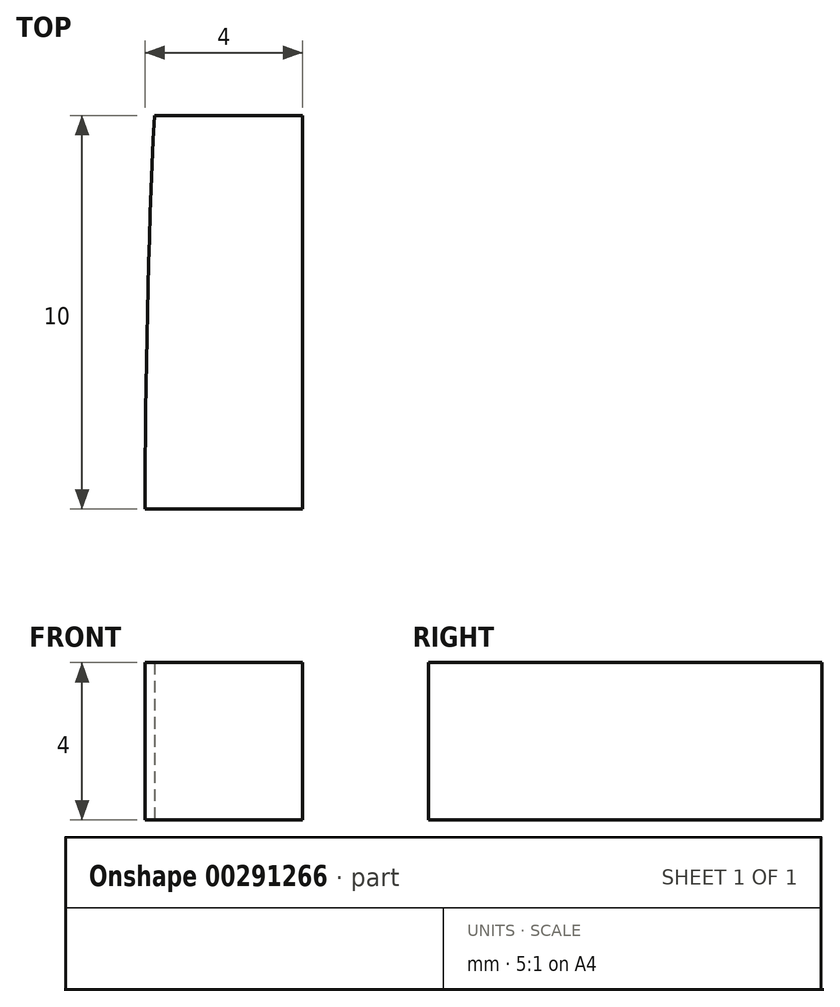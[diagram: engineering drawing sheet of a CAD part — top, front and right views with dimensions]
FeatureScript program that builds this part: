
annotation { "Feature Type Name" : "Feature", "Feature Type Description" : "" }
export const myFeature = defineFeature(function(context is Context, id is Id, definition is map)
    precondition{}
    {
        {
            var Q0;
            Q0=qCreatedBy(makeId("Top.planeOp"),FACE);
            var sketch = newSketch(context, id + "F0", { "sketchPlane" : qUnion([Q0])});
            skArc(sketch, "E0", {"start": v(-134.47, 163.78) * mm, "mid": v(-211.91, 0) * mm, "end": v(-134.47, -163.78) * mm});
            skLineSegment(sketch, "E1.bottom", {"start": v(-134.47, -163.78) * mm, "end": v(-132, -163.78) * mm});
            skLineSegment(sketch, "E1.top", {"start": v(-134.47, 163.78) * mm, "end": v(-132, 163.78) * mm});
            skArc(sketch, "E2.trimOffspring", {"start": v(134.47, -163.78) * mm, "mid": v(211.91, 0) * mm, "end": v(134.47, 163.78) * mm});
            skPoint(sketch, "E1.right.start.orphan", {"position": v(234.51, -163.78) * mm});
            skPoint(sketch, "E3.orphan", {"position": v(234.51, 163.78) * mm});
            skPoint(sketch, "E1.left.end.orphan", {"position": v(-234.51, 163.78) * mm});
            skPoint(sketch, "E4.orphan", {"position": v(-234.51, -163.78) * mm});
            skLineSegment(sketch, "E5.bottom", {"start": v(-40, 120) * mm, "end": v(40, 120) * mm});
            skLineSegment(sketch, "E5.top", {"start": v(-40, 140) * mm, "end": v(40, 140) * mm});
            skLineSegment(sketch, "E5.left", {"start": v(-40, 120) * mm, "end": v(-40, 140) * mm});
            skLineSegment(sketch, "E5.right", {"start": v(40, 120) * mm, "end": v(40, 140) * mm});
            skPoint(sketch, "E5.middle", {"position": v(0, 130) * mm});
            skLineSegment(sketch, "E6.bottom", {"start": v(-40, -140) * mm, "end": v(40, -140) * mm});
            skLineSegment(sketch, "E6.top", {"start": v(-40, -120) * mm, "end": v(40, -120) * mm});
            skLineSegment(sketch, "E6.left", {"start": v(-40, -140) * mm, "end": v(-40, -120) * mm});
            skLineSegment(sketch, "E6.right", {"start": v(40, -140) * mm, "end": v(40, -120) * mm});
            skPoint(sketch, "E6.middle", {"position": v(0, -130) * mm});
            skLineSegment(sketch, "E7", {"start": v(0, 163.78) * mm, "end": v(0, 159.78) * mm});
            skPoint(sketch, "E7.endSnap0", {"position": v(0, 163.78) * mm});
            skLineSegment(sketch, "E8", {"start": v(0, 159.78) * mm, "end": v(15, 159.78) * mm});
            skLineSegment(sketch, "E9", {"start": v(15, 159.78) * mm, "end": v(15, 163.78) * mm});
            skLineSegment(sketch, "E10.1.0.0", {"start": v(34.4, 159.78) * mm, "end": v(34.4, 163.78) * mm});
            skLineSegment(sketch, "E10.1.0.1", {"start": v(19.4, 159.78) * mm, "end": v(34.4, 159.78) * mm});
            skLineSegment(sketch, "E10.1.0.2", {"start": v(19.4, 163.78) * mm, "end": v(19.4, 159.78) * mm});
            skLineSegment(sketch, "E10.2.0.0", {"start": v(53.8, 159.78) * mm, "end": v(53.8, 163.78) * mm});
            skLineSegment(sketch, "E10.2.0.1", {"start": v(38.8, 159.78) * mm, "end": v(53.8, 159.78) * mm});
            skLineSegment(sketch, "E10.2.0.2", {"start": v(38.8, 163.78) * mm, "end": v(38.8, 159.78) * mm});
            skLineSegment(sketch, "E10.3.0.0", {"start": v(73.2, 159.78) * mm, "end": v(73.2, 163.78) * mm});
            skLineSegment(sketch, "E10.3.0.1", {"start": v(58.2, 159.78) * mm, "end": v(73.2, 159.78) * mm});
            skLineSegment(sketch, "E10.3.0.2", {"start": v(58.2, 163.78) * mm, "end": v(58.2, 159.78) * mm});
            skLineSegment(sketch, "E10.4.0.0", {"start": v(92.6, 159.78) * mm, "end": v(92.6, 163.78) * mm});
            skLineSegment(sketch, "E10.4.0.1", {"start": v(77.6, 159.78) * mm, "end": v(92.6, 159.78) * mm});
            skLineSegment(sketch, "E10.4.0.2", {"start": v(77.6, 163.78) * mm, "end": v(77.6, 159.78) * mm});
            skLineSegment(sketch, "E10.5.0.0", {"start": v(112, 159.78) * mm, "end": v(112, 163.78) * mm});
            skLineSegment(sketch, "E10.5.0.1", {"start": v(97, 159.78) * mm, "end": v(112, 159.78) * mm});
            skLineSegment(sketch, "E10.5.0.2", {"start": v(97, 163.78) * mm, "end": v(97, 159.78) * mm});
            skLineSegment(sketch, "E10.6.0.0", {"start": v(131.4, 159.78) * mm, "end": v(131.4, 163.78) * mm});
            skLineSegment(sketch, "E10.6.0.1", {"start": v(116.4, 159.78) * mm, "end": v(131.4, 159.78) * mm});
            skLineSegment(sketch, "E10.6.0.2", {"start": v(116.4, 163.78) * mm, "end": v(116.4, 159.78) * mm});
            skLineSegment(sketch, "E10.direction1", {"start": v(15, 159.78) * mm, "end": v(34.4, 159.78) * mm, "construction": true});
            skLineSegment(sketch, "E11.1.0.0", {"start": v(-7, 159.78) * mm, "end": v(-7, 163.78) * mm});
            skLineSegment(sketch, "E11.1.0.1", {"start": v(-22, 159.78) * mm, "end": v(-7, 159.78) * mm});
            skLineSegment(sketch, "E11.1.0.2", {"start": v(-22, 163.78) * mm, "end": v(-22, 159.78) * mm});
            skLineSegment(sketch, "E11.2.0.0", {"start": v(-29, 159.78) * mm, "end": v(-29, 163.78) * mm});
            skLineSegment(sketch, "E11.2.0.1", {"start": v(-44, 159.78) * mm, "end": v(-29, 159.78) * mm});
            skLineSegment(sketch, "E11.2.0.2", {"start": v(-44, 163.78) * mm, "end": v(-44, 159.78) * mm});
            skLineSegment(sketch, "E11.3.0.0", {"start": v(-51, 159.78) * mm, "end": v(-51, 163.78) * mm});
            skLineSegment(sketch, "E11.3.0.1", {"start": v(-66, 159.78) * mm, "end": v(-51, 159.78) * mm});
            skLineSegment(sketch, "E11.3.0.2", {"start": v(-66, 163.78) * mm, "end": v(-66, 159.78) * mm});
            skLineSegment(sketch, "E11.4.0.0", {"start": v(-73, 159.78) * mm, "end": v(-73, 163.78) * mm});
            skLineSegment(sketch, "E11.4.0.1", {"start": v(-88, 159.78) * mm, "end": v(-73, 159.78) * mm});
            skLineSegment(sketch, "E11.4.0.2", {"start": v(-88, 163.78) * mm, "end": v(-88, 159.78) * mm});
            skLineSegment(sketch, "E11.5.0.0", {"start": v(-95, 159.78) * mm, "end": v(-95, 163.78) * mm});
            skLineSegment(sketch, "E11.5.0.1", {"start": v(-110, 159.78) * mm, "end": v(-95, 159.78) * mm});
            skLineSegment(sketch, "E11.5.0.2", {"start": v(-110, 163.78) * mm, "end": v(-110, 159.78) * mm});
            skLineSegment(sketch, "E11.6.0.0", {"start": v(-117, 159.78) * mm, "end": v(-117, 163.78) * mm});
            skLineSegment(sketch, "E11.6.0.1", {"start": v(-132, 159.78) * mm, "end": v(-117, 159.78) * mm});
            skLineSegment(sketch, "E11.6.0.2", {"start": v(-132, 163.78) * mm, "end": v(-132, 159.78) * mm});
            skLineSegment(sketch, "E11.direction1", {"start": v(15, 159.78) * mm, "end": v(-7, 159.78) * mm, "construction": true});
            skLineSegment(sketch, "E12.trimOffspring", {"start": v(-117, 163.78) * mm, "end": v(-110, 163.78) * mm});
            skLineSegment(sketch, "E13.trimOffspring", {"start": v(-95, 163.78) * mm, "end": v(-88, 163.78) * mm});
            skLineSegment(sketch, "E14.trimOffspring", {"start": v(-73, 163.78) * mm, "end": v(-66, 163.78) * mm});
            skLineSegment(sketch, "E15.trimOffspring", {"start": v(-51, 163.78) * mm, "end": v(-44, 163.78) * mm});
            skLineSegment(sketch, "E16.trimOffspring", {"start": v(-29, 163.78) * mm, "end": v(-22, 163.78) * mm});
            skLineSegment(sketch, "E17.trimOffspring", {"start": v(-7, 163.78) * mm, "end": v(0, 163.78) * mm});
            skLineSegment(sketch, "E18.trimOffspring", {"start": v(15, 163.78) * mm, "end": v(19.4, 163.78) * mm});
            skLineSegment(sketch, "E19.trimOffspring", {"start": v(34.4, 163.78) * mm, "end": v(38.8, 163.78) * mm});
            skLineSegment(sketch, "E20.trimOffspring", {"start": v(53.8, 163.78) * mm, "end": v(58.2, 163.78) * mm});
            skLineSegment(sketch, "E21.trimOffspring", {"start": v(73.2, 163.78) * mm, "end": v(77.6, 163.78) * mm});
            skLineSegment(sketch, "E22.trimOffspring", {"start": v(92.6, 163.78) * mm, "end": v(97, 163.78) * mm});
            skLineSegment(sketch, "E23.trimOffspring", {"start": v(131.4, 163.78) * mm, "end": v(134.47, 163.78) * mm});
            skLineSegment(sketch, "E24.trimOffspring", {"start": v(112, 163.78) * mm, "end": v(116.4, 163.78) * mm});
            skLineSegment(sketch, "E25", {"start": v(-211.91, 0) * mm, "end": v(211.91, 0) * mm});
            skLineSegment(sketch, "E26.MirrorCS", {"start": v(-7, -163.78) * mm, "end": v(0, -163.78) * mm});
            skLineSegment(sketch, "E27.MirrorCS", {"start": v(77.6, -163.78) * mm, "end": v(77.6, -159.78) * mm});
            skLineSegment(sketch, "E28.MirrorCS", {"start": v(-66, -163.78) * mm, "end": v(-66, -159.78) * mm});
            skLineSegment(sketch, "E29.MirrorCS", {"start": v(-132, -163.78) * mm, "end": v(-132, -159.78) * mm});
            skLineSegment(sketch, "E30.MirrorCS", {"start": v(15, -163.78) * mm, "end": v(19.4, -163.78) * mm});
            skLineSegment(sketch, "E31.MirrorCS", {"start": v(-73, -159.78) * mm, "end": v(-73, -163.78) * mm});
            skLineSegment(sketch, "E32.MirrorCS", {"start": v(112, -159.78) * mm, "end": v(112, -163.78) * mm});
            skLineSegment(sketch, "E33.MirrorCS", {"start": v(38.8, -163.78) * mm, "end": v(38.8, -159.78) * mm});
            skLineSegment(sketch, "E34.MirrorCS", {"start": v(53.8, -163.78) * mm, "end": v(58.2, -163.78) * mm});
            skLineSegment(sketch, "E35.MirrorCS", {"start": v(-88, -163.78) * mm, "end": v(-88, -159.78) * mm});
            skLineSegment(sketch, "E36.MirrorCS", {"start": v(97, -163.78) * mm, "end": v(97, -159.78) * mm});
            skLineSegment(sketch, "E37.MirrorCS", {"start": v(-22, -163.78) * mm, "end": v(-22, -159.78) * mm});
            skLineSegment(sketch, "E38.MirrorCS", {"start": v(34.4, -163.78) * mm, "end": v(38.8, -163.78) * mm});
            skLineSegment(sketch, "E39.MirrorCS", {"start": v(73.2, -159.78) * mm, "end": v(73.2, -163.78) * mm});
            skLineSegment(sketch, "E40.MirrorCS", {"start": v(73.2, -163.78) * mm, "end": v(77.6, -163.78) * mm});
            skLineSegment(sketch, "E41.MirrorCS", {"start": v(-117, -163.78) * mm, "end": v(-110, -163.78) * mm});
            skLineSegment(sketch, "E42.MirrorCS", {"start": v(-95, -159.78) * mm, "end": v(-95, -163.78) * mm});
            skLineSegment(sketch, "E43.MirrorCS", {"start": v(131.4, -159.78) * mm, "end": v(131.4, -163.78) * mm});
            skLineSegment(sketch, "E44.MirrorCS", {"start": v(-29, -159.78) * mm, "end": v(-29, -163.78) * mm});
            skLineSegment(sketch, "E45.MirrorCS", {"start": v(92.6, -163.78) * mm, "end": v(97, -163.78) * mm});
            skLineSegment(sketch, "E46.MirrorCS", {"start": v(-95, -163.78) * mm, "end": v(-88, -163.78) * mm});
            skLineSegment(sketch, "E47.MirrorCS", {"start": v(15, -159.78) * mm, "end": v(15, -163.78) * mm});
            skLineSegment(sketch, "E48.MirrorCS", {"start": v(34.4, -159.78) * mm, "end": v(34.4, -163.78) * mm});
            skLineSegment(sketch, "E49.MirrorCS", {"start": v(0, -163.78) * mm, "end": v(0, -159.78) * mm});
            skLineSegment(sketch, "E50.MirrorCS", {"start": v(-44, -163.78) * mm, "end": v(-44, -159.78) * mm});
            skLineSegment(sketch, "E51.MirrorCS", {"start": v(-73, -163.78) * mm, "end": v(-66, -163.78) * mm});
            skLineSegment(sketch, "E52.MirrorCS", {"start": v(58.2, -163.78) * mm, "end": v(58.2, -159.78) * mm});
            skLineSegment(sketch, "E53.MirrorCS", {"start": v(-110, -163.78) * mm, "end": v(-110, -159.78) * mm});
            skLineSegment(sketch, "E54.MirrorCS", {"start": v(131.4, -163.78) * mm, "end": v(134.47, -163.78) * mm});
            skLineSegment(sketch, "E55.MirrorCS", {"start": v(116.4, -163.78) * mm, "end": v(116.4, -159.78) * mm});
            skLineSegment(sketch, "E56.MirrorCS", {"start": v(-51, -163.78) * mm, "end": v(-44, -163.78) * mm});
            skLineSegment(sketch, "E57.MirrorCS", {"start": v(92.6, -159.78) * mm, "end": v(92.6, -163.78) * mm});
            skLineSegment(sketch, "E58.MirrorCS", {"start": v(-51, -159.78) * mm, "end": v(-51, -163.78) * mm});
            skLineSegment(sketch, "E59.MirrorCS", {"start": v(19.4, -163.78) * mm, "end": v(19.4, -159.78) * mm});
            skLineSegment(sketch, "E60.MirrorCS", {"start": v(-117, -159.78) * mm, "end": v(-117, -163.78) * mm});
            skLineSegment(sketch, "E61.MirrorCS", {"start": v(112, -163.78) * mm, "end": v(116.4, -163.78) * mm});
            skLineSegment(sketch, "E62.MirrorCS", {"start": v(-29, -163.78) * mm, "end": v(-22, -163.78) * mm});
            skLineSegment(sketch, "E63.MirrorCS", {"start": v(53.8, -159.78) * mm, "end": v(53.8, -163.78) * mm});
            skLineSegment(sketch, "E64.MirrorCS", {"start": v(-7, -159.78) * mm, "end": v(-7, -163.78) * mm});
            skLineSegment(sketch, "E65.MirrorCS", {"start": v(0, -159.78) * mm, "end": v(15, -159.78) * mm});
            skLineSegment(sketch, "E66.MirrorCS", {"start": v(19.4, -159.78) * mm, "end": v(34.4, -159.78) * mm});
            skLineSegment(sketch, "E67.MirrorCS", {"start": v(38.8, -159.78) * mm, "end": v(53.8, -159.78) * mm});
            skLineSegment(sketch, "E68.MirrorCS", {"start": v(-22, -159.78) * mm, "end": v(-7, -159.78) * mm});
            skLineSegment(sketch, "E69.MirrorCS", {"start": v(15, -159.78) * mm, "end": v(-7, -159.78) * mm, "construction": true});
            skLineSegment(sketch, "E70.MirrorCS", {"start": v(-88, -159.78) * mm, "end": v(-73, -159.78) * mm});
            skLineSegment(sketch, "E71.MirrorCS", {"start": v(97, -159.78) * mm, "end": v(112, -159.78) * mm});
            skLineSegment(sketch, "E72.MirrorCS", {"start": v(58.2, -159.78) * mm, "end": v(73.2, -159.78) * mm});
            skPoint(sketch, "E73.MirrorP", {"position": v(0, -163.78) * mm});
            skLineSegment(sketch, "E74.MirrorCS", {"start": v(116.4, -159.78) * mm, "end": v(131.4, -159.78) * mm});
            skLineSegment(sketch, "E75.MirrorCS", {"start": v(-110, -159.78) * mm, "end": v(-95, -159.78) * mm});
            skLineSegment(sketch, "E76.MirrorCS", {"start": v(-44, -159.78) * mm, "end": v(-29, -159.78) * mm});
            skLineSegment(sketch, "E77.MirrorCS", {"start": v(15, -159.78) * mm, "end": v(34.4, -159.78) * mm, "construction": true});
            skLineSegment(sketch, "E78.MirrorCS", {"start": v(-66, -159.78) * mm, "end": v(-51, -159.78) * mm});
            skLineSegment(sketch, "E79.MirrorCS", {"start": v(77.6, -159.78) * mm, "end": v(92.6, -159.78) * mm});
            skLineSegment(sketch, "E80.MirrorCS", {"start": v(-132, -159.78) * mm, "end": v(-117, -159.78) * mm});
            skLineSegment(sketch, "E81", {"start": v(-211.91, 0) * mm, "end": v(-207.91, 0) * mm});
            skLineSegment(sketch, "E82", {"start": v(-207.91, 0) * mm, "end": v(-207.91, 10) * mm});
            skLineSegment(sketch, "E83", {"start": v(-207.91, 10) * mm, "end": v(-211.67, 10) * mm});
            skSolve(sketch);
        }
        {
            var Q0;
            Q0=makeQuery(id+"F0.imprint","IMPRINT",FACE,{"disambiguationData":[TD([[makeQuery(id+"F0.imprint","IMPRINT",EDGE,{"derivedFrom":sQuery(id+"F0.wireOp",EDGE,"E0")}),1.0]])]});
            extrude(context, id + "F1", {"entities" : qUnion([Q0]), "depth" : 4 * mm});
        }
    });
